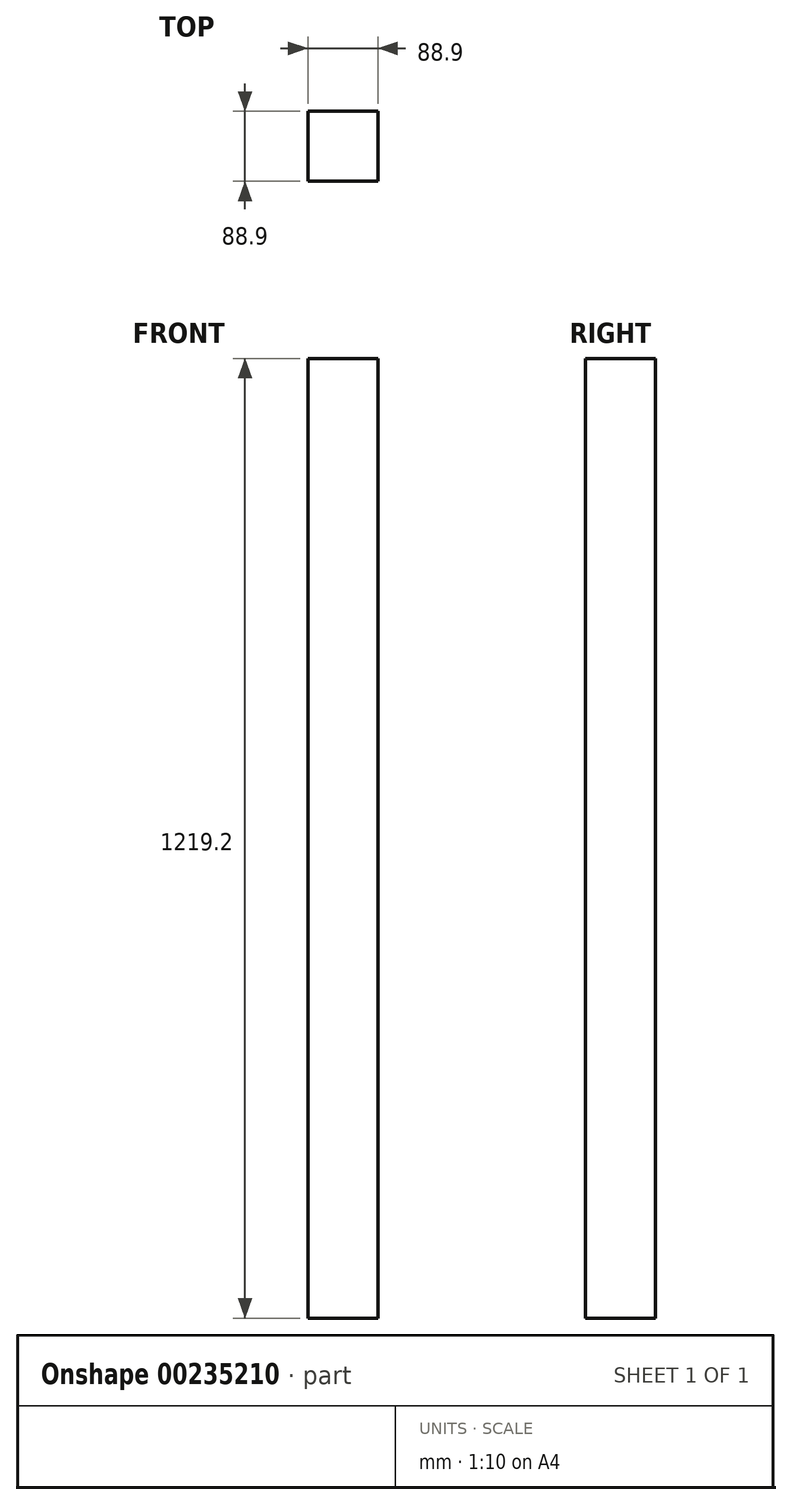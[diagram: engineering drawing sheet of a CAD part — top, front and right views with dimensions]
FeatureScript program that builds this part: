
annotation { "Feature Type Name" : "Feature", "Feature Type Description" : "" }
export const myFeature = defineFeature(function(context is Context, id is Id, definition is map)
    precondition{}
    {
        {
            var Q0;
            Q0=qCreatedBy(makeId("Top.planeOp"),FACE);
            var sketch = newSketch(context, id + "F0", { "sketchPlane" : qUnion([Q0])});
            skLineSegment(sketch, "E0.bottom", {"start": v(44.45, 44.45) * mm, "end": v(-44.45, 44.45) * mm});
            skLineSegment(sketch, "E0.top", {"start": v(44.45, -44.45) * mm, "end": v(-44.45, -44.45) * mm});
            skLineSegment(sketch, "E0.left", {"start": v(44.45, 44.45) * mm, "end": v(44.45, -44.45) * mm});
            skLineSegment(sketch, "E0.right", {"start": v(-44.45, 44.45) * mm, "end": v(-44.45, -44.45) * mm});
            skPoint(sketch, "E0.middle", {"position": v(0, 0) * mm});
            skSolve(sketch);
        }
        {
            var Q0;
            Q0=makeQuery(id+"F0.imprint","IMPRINT",FACE,{"disambiguationData":[TD([[makeQuery(id+"F0.imprint","IMPRINT",EDGE,{"derivedFrom":sQuery(id+"F0.wireOp",EDGE,"E0.bottom")}),1.0]])]});
            extrude(context, id + "F1", {"entities" : qUnion([Q0]), "depth" : 1219.2 * mm});
        }
    });
